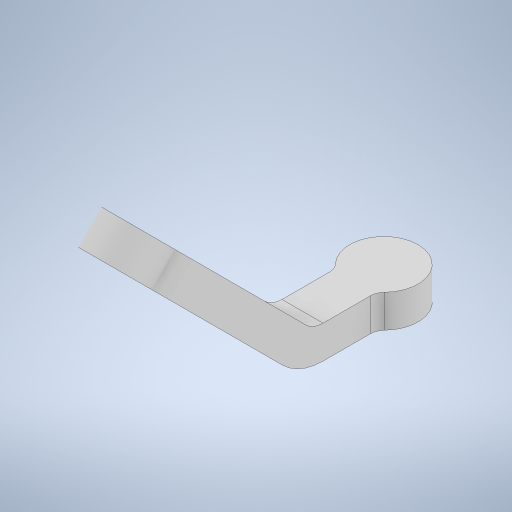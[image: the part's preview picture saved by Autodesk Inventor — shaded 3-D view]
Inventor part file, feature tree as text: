
AUTODESK INVENTOR PART (.ipt)
format: ipt  version: 2024 (Build 280153000, 153)  size: 320,000 bytes
history: native  units: mm
features: sketch x7, extrude x5, other x3, sweep x1, plane x1, mirror x1
ambient origin geometry x8: Origin, YZ Plane, XZ Plane, XY Plane, X Axis, Y Axis, Z Axis, Center Point
bodies: Solid1 (feature_tree)
feature tree (18):
  extrude  "Extrusion1"  Depth=12.0mm TaperAngle=0.0deg
  sweep  "Sweep2"
  plane  "Work Plane11"
  extrude  "Extrusion17"  Depth=5.0mm
  extrude  "Extrusion18"  Depth=70.0mm
  other  "Work Point1"
  extrude  "Extrusion19"  Depth=15.0mm
  extrude  "Extrusion20"  [1 undecoded]
  mirror  "Mirror2"
  sketch  "Sketch1"  dims[d0=25.0mm d1=12.0mm d2=0.0mm]
  sketch  "Sketch22"  dims[d106=15.0mm d107=10.0mm]
  sketch  "Sketch23"  dims[d108=10.0mm d109=5.0mm]
  sketch  "Sketch24"  dims[d110=15.919313mm d111=70.0mm]
  sketch  "Sketch25"  dims[d112=135.0deg d113=15.0mm]
  other  "Work Axis1"
  other  "Work Axis2"
  sketch  "Sketch26"  dims[d114=0.0mm d115=0.0mm d116=-6.0mm]
  sketch  "Sketch27"  dims[d121=12.0mm d122=0.0mm d123=5.0mm d124=0.0mm d125=0.0mm d126=15.2mm d127=5.0mm d128=0.0mm d129=22.0mm d130=12.0mm d131=16.2mm d132=5.0mm d133=0.0mm d74=0.5mm d75=0.872665mm d76=0.5mm d77=0.872665mm d98=0.0mm d99=0.0mm d100=0.0mm d101=0.0mm d102=0.872665mm d103=0.5mm d104=0.872665mm]
note: 1 required parameter value undecoded (feature->parameter linkage not recoverable at this tier; creation-order binding heuristic only, values carry confidence <= 0.55)
